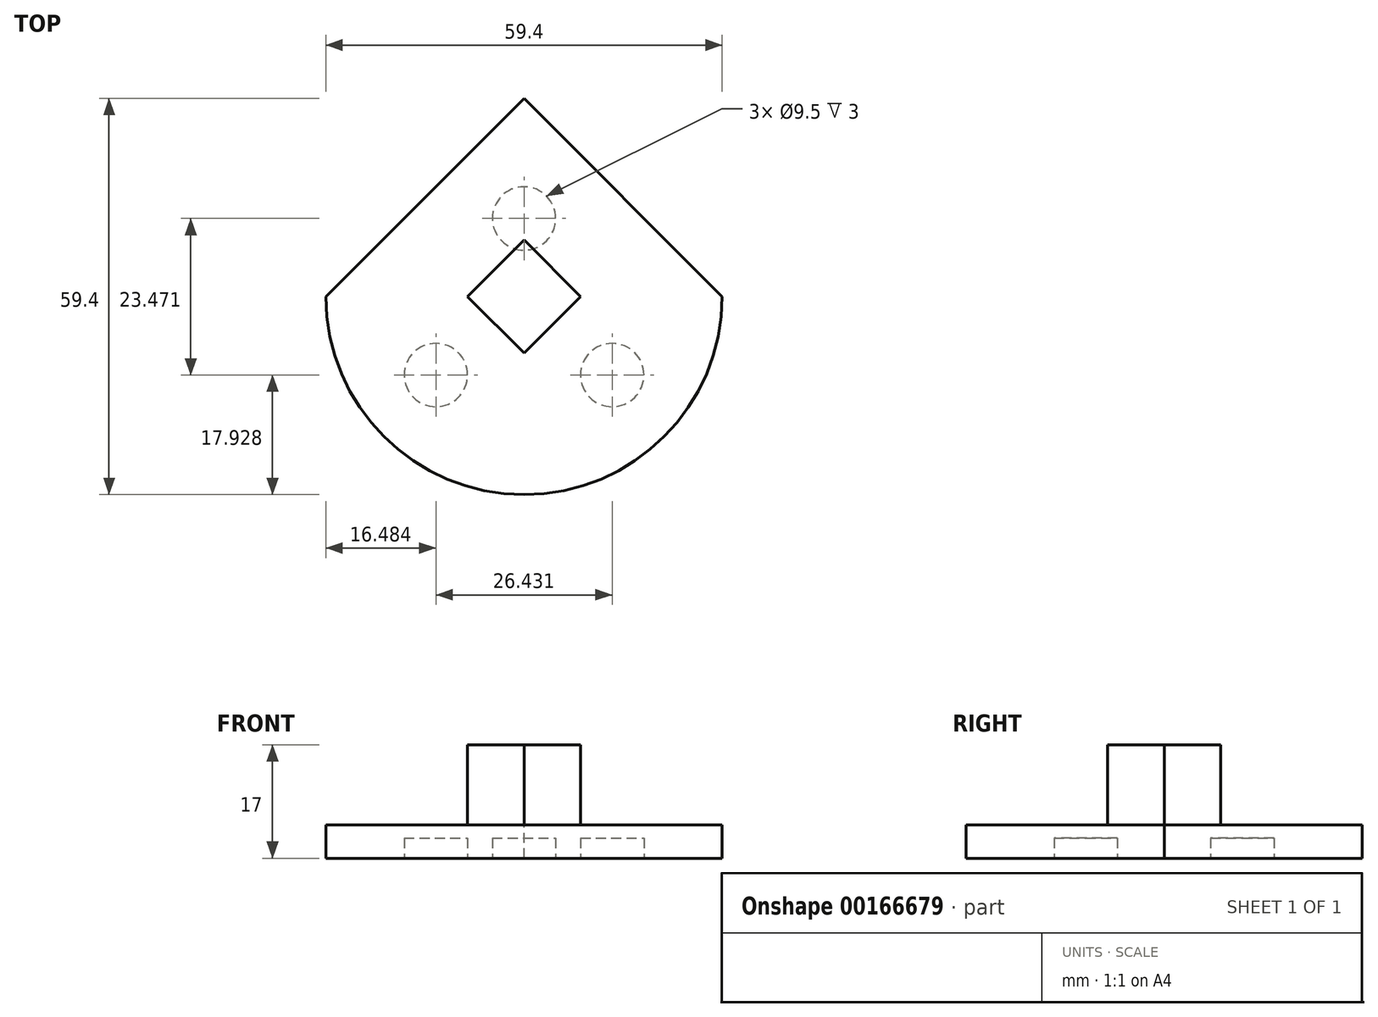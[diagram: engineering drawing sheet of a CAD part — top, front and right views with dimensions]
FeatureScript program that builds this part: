
annotation { "Feature Type Name" : "Feature", "Feature Type Description" : "" }
export const myFeature = defineFeature(function(context is Context, id is Id, definition is map)
    precondition{}
    {
        {
            assignVariable(context, id + "F0", {"name" : "cube", "anyValue" : 12});
        }
        {
            var Q0;
            Q0=qCreatedBy(makeId("Top.planeOp"),FACE);
            var sketch = newSketch(context, id + "F1", { "sketchPlane" : qUnion([Q0])});
            skLineSegment(sketch, "E0.bottom", {"start": v(0, -8.49) * mm, "end": v(-8.49, 0) * mm});
            skLineSegment(sketch, "E0.top", {"start": v(8.49, 0) * mm, "end": v(0, 8.49) * mm});
            skLineSegment(sketch, "E0.left", {"start": v(0, -8.49) * mm, "end": v(8.49, 0) * mm});
            skLineSegment(sketch, "E0.right", {"start": v(-8.49, 0) * mm, "end": v(0, 8.49) * mm});
            skPoint(sketch, "E0.middle", {"position": v(0, 0) * mm});
            skSolve(sketch);
        }
        {
            var Q0;
            Q0 = qSketchRegion(id + "F1", true);
            extrude(context, id + "F2", {"entities" : qUnion([Q0]), "depth" : getVariable(context, 'cube') * mm});
        }
        {
            var Q0;
            Q0=qCreatedBy(makeId("Top.planeOp"),FACE);
            var sketch = newSketch(context, id + "F3", { "sketchPlane" : qUnion([Q0])});
            skLineSegment(sketch, "E1", {"start": v(-29.7, 0) * mm, "end": v(0, 29.7) * mm});
            skLineSegment(sketch, "E2", {"start": v(0, 29.7) * mm, "end": v(29.7, 0) * mm});
            skArc(sketch, "E3", {"start": v(-29.7, 0) * mm, "mid": v(0, -29.7) * mm, "end": v(29.7, 0) * mm});
            skSolve(sketch);
        }
        {
            var Q0;
            Q0 = qSketchRegion(id + "F3", true);
            extrude(context, id + "F4", {"entities" : qUnion([Q0]), "operationType" : NewBodyOperationType.ADD, "oppositeDirection" : true, "depth" : 5 * mm});
        }
        {
            var Q0;
            Q0=makeQuery(id+"F4.opExtrude","CAP_FACE",FACE,{"disambiguationData":[OSD([sQuery(id+"F3.wireOp",EDGE,"E1"),sQuery(id+"F3.wireOp",EDGE,"E2"),sQuery(id+"F3.wireOp",EDGE,"E3")])],"isStart":false});
            var sketch = newSketch(context, id + "F5", { "sketchPlane" : qUnion([Q0])});
            skCircle(sketch, "E4", {"center": v(0, -11.7) * mm, "radius": 4.75 * mm});
            skCircle(sketch, "E5", {"center": v(-13.22, 11.77) * mm, "radius": 4.75 * mm});
            skCircle(sketch, "E6", {"center": v(13.22, 11.77) * mm, "radius": 4.75 * mm});
            skSolve(sketch);
        }
        {
            var Q0;
            Q0 = qSketchRegion(id + "F5", true);
            extrude(context, id + "F6", {"entities" : qUnion([Q0]), "operationType" : NewBodyOperationType.REMOVE, "oppositeDirection" : true, "depth" : 3 * mm});
        }
    });
